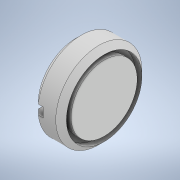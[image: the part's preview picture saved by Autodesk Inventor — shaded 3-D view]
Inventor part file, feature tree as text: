
AUTODESK INVENTOR PART (.ipt)
format: ipt  version: 2022 (Build 260153000, 153)  size: 152,576 bytes
history: native  units: mm
features: sketch x4, other x2, revolve x2, extrude x1, hole x1
ambient origin geometry x8: Origin, YZ Plane, XZ Plane, XY Plane, X Axis, Y Axis, Z Axis, Center Point
bodies: Body1 (feature_tree)
feature tree (10):
  other  "Твердое тело1"
  revolve  "Вращение1"
  other  "РабПлоскость1"
  extrude  "Выдавливание1"  Depth=20.0mm
  hole  "Отверстие1"  [1 undecoded]
  revolve  "Вращение2"
  sketch  "Эскиз1"
  sketch  "Эскиз2"
  sketch  "Эскиз3"
  sketch  "Эскиз4"
note: 1 required parameter value undecoded (feature->parameter linkage not recoverable at this tier; creation-order binding heuristic only, values carry confidence <= 0.55)
